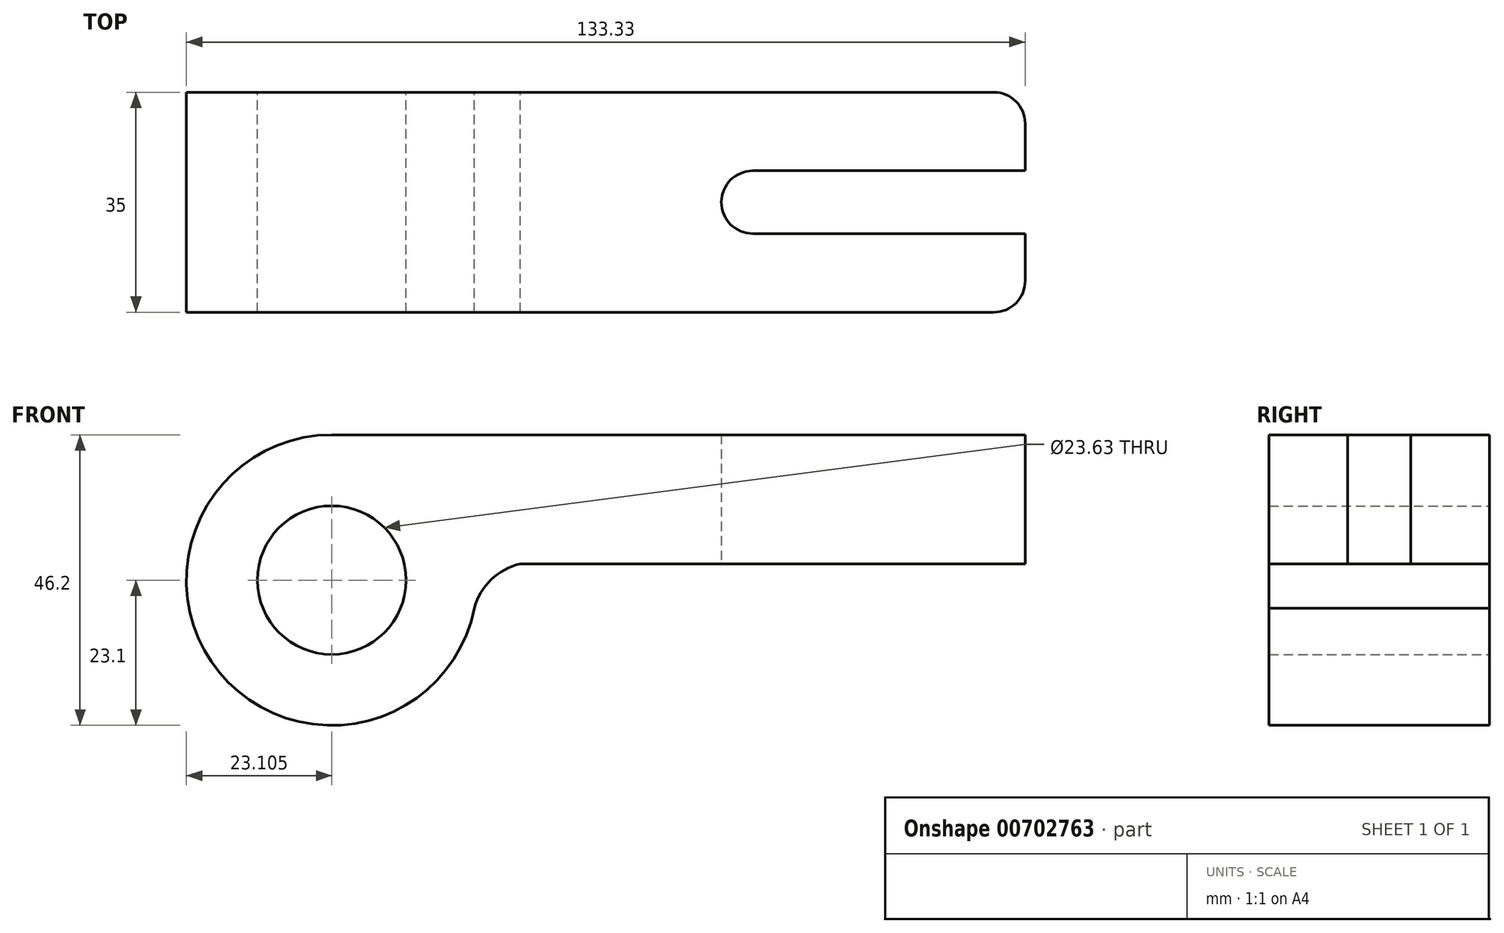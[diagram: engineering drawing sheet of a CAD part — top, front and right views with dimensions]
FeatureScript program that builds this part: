
annotation { "Feature Type Name" : "Feature", "Feature Type Description" : "" }
export const myFeature = defineFeature(function(context is Context, id is Id, definition is map)
    precondition{}
    {
        {
            var Q0;
            Q0=qCreatedBy(makeId("Front.planeOp"),FACE);
            var sketch = newSketch(context, id + "F0", { "sketchPlane" : qUnion([Q0])});
            skCircle(sketch, "E0", {"center": v(-63.09, 0) * mm, "radius": 11.82 * mm});
            skArc(sketch, "E1", {"start": v(-63.08, 23.1) * mm, "mid": v(-80.93, -14.68) * mm, "end": v(-40.41, -4.45) * mm});
            skLineSegment(sketch, "E2", {"start": v(-63.08, 23.1) * mm, "end": v(47.14, 23.1) * mm});
            skLineSegment(sketch, "E3", {"start": v(-33.11, 2.6) * mm, "end": v(47.14, 2.6) * mm});
            skLineSegment(sketch, "E4", {"start": v(47.14, 23.1) * mm, "end": v(47.14, 2.6) * mm});
            skArc(sketch, "E5", {"start": v(-33.11, 2.6) * mm, "mid": v(-37.74, 0.1) * mm, "end": v(-40.41, -4.45) * mm});
            skSolve(sketch);
        }
        {
            var Q0;
            Q0 = qSketchRegion(id + "F0", true);
            extrude(context, id + "F1", {"entities" : qUnion([Q0]), "depth" : 35 * mm, "offsetDistance" : 25 * mm});
        }
        {
            var Q0;
            Q0=makeQuery(id+"F1.opExtrude","CAP_EDGE",EDGE,{"disambiguationData":[OSD([sQuery(id+"F0.wireOp",EDGE,"E4")])],"isStart":false});
            var Q1;
            Q1=makeQuery(id+"F1.opExtrude","CAP_EDGE",EDGE,{"disambiguationData":[OSD([sQuery(id+"F0.wireOp",EDGE,"E4")])],"isStart":true});
            fillet(context, id + "F2", {"entities" : qUnion([Q0, Q1]), "radius" : 5 * mm, "tangentPropagation" : true, "allowEdgeOverflow" : false});
        }
        {
            var Q0;
            Q0=makeQuery(id+"F1.opExtrude","SWEPT_FACE",FACE,{"disambiguationData":[OSD([sQuery(id+"F0.wireOp",EDGE,"E3")])]});
            var sketch = newSketch(context, id + "F3", { "sketchPlane" : qUnion([Q0])});
            skLineSegment(sketch, "E6.bottom", {"start": v(47.14, 22.5) * mm, "end": v(3.86, 22.5) * mm});
            skLineSegment(sketch, "E6.top", {"start": v(47.14, 12.5) * mm, "end": v(3.86, 12.5) * mm});
            skPoint(sketch, "E7.end.orphan", {"position": v(3.86, 17.5) * mm});
            skPoint(sketch, "E8.end.orphan", {"position": v(47.14, 12.5) * mm});
            skPoint(sketch, "E8.start.orphan", {"position": v(47.14, 17.5) * mm});
            skArc(sketch, "E9", {"start": v(3.86, 22.5) * mm, "mid": v(-1.14, 17.5) * mm, "end": v(3.86, 12.5) * mm});
            skSolve(sketch);
        }
        {
            var Q0;
            {var subQ0=sQuery(id+"F3.wireOp",EDGE,"E6.bottom");Q0=makeQuery(id+"F3.imprint","IMPRINT",FACE,{"disambiguationData":[TD([[makeQuery(id+"F3.imprint","IMPRINT",EDGE,{"derivedFrom":subQ0}),1.0]])]});}
            extrude(context, id + "F4", {"entities" : qUnion([Q0]), "operationType" : NewBodyOperationType.REMOVE, "oppositeDirection" : true, "depth" : 40 * mm, "offsetDistance" : 25 * mm});
        }
    });
